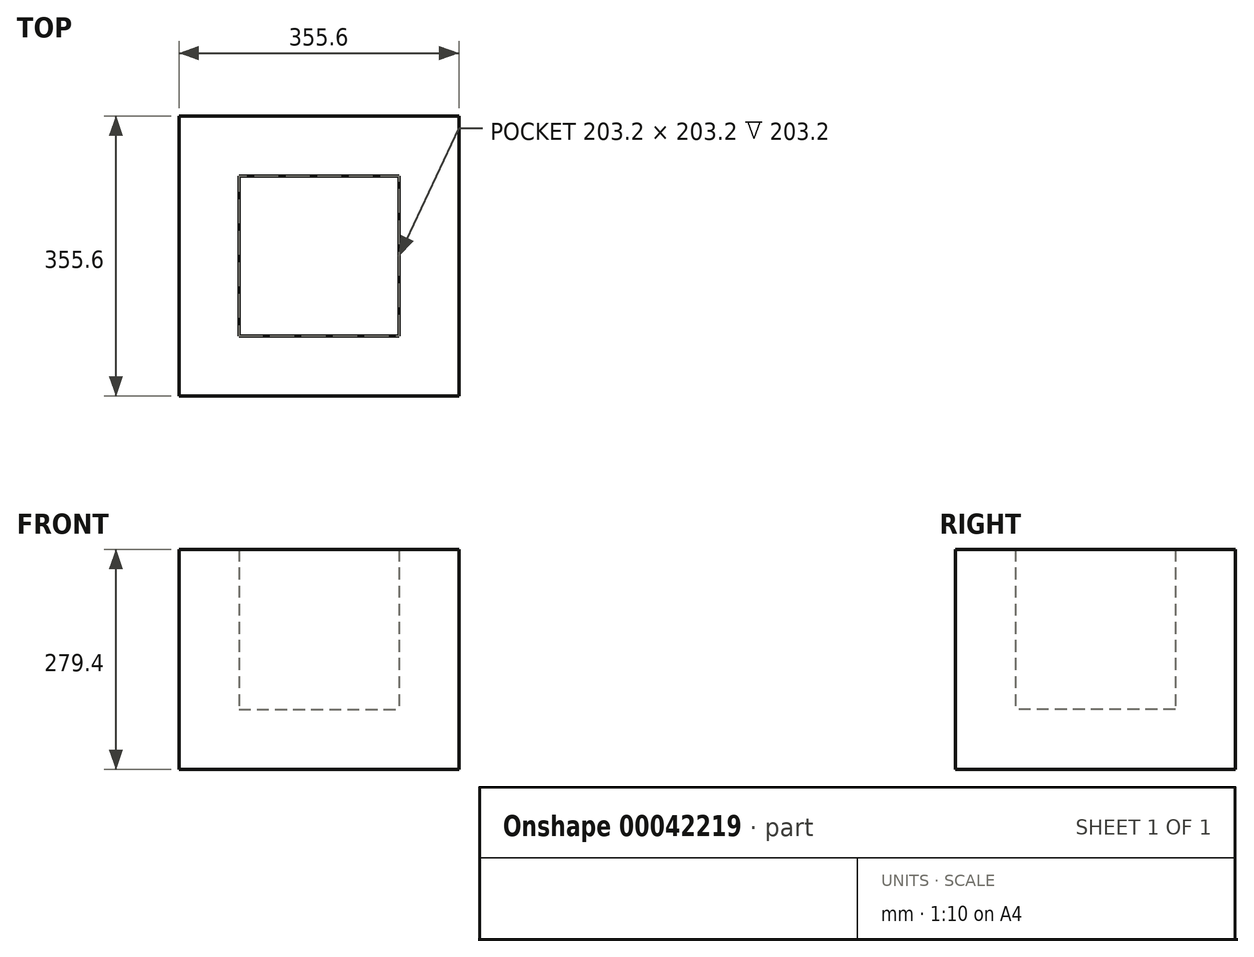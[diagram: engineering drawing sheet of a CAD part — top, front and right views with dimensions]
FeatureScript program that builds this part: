
annotation { "Feature Type Name" : "Feature", "Feature Type Description" : "" }
export const myFeature = defineFeature(function(context is Context, id is Id, definition is map)
    precondition{}
    {
        {
            var Q0;
            Q0=qCreatedBy(makeId("Top.planeOp"),FACE);
            var sketch = newSketch(context, id + "F0", { "sketchPlane" : qUnion([Q0])});
            skLineSegment(sketch, "E0.bottom", {"start": v(-154.17, 102.23) * mm, "end": v(49.03, 102.23) * mm});
            skLineSegment(sketch, "E0.top", {"start": v(-154.17, -100.97) * mm, "end": v(49.03, -100.97) * mm});
            skLineSegment(sketch, "E0.left", {"start": v(-154.17, 102.23) * mm, "end": v(-154.17, -100.97) * mm});
            skLineSegment(sketch, "E0.right", {"start": v(49.03, 102.23) * mm, "end": v(49.03, -100.97) * mm});
            skLineSegment(sketch, "E1.bottom", {"start": v(-230.37, 178.43) * mm, "end": v(125.23, 178.43) * mm});
            skLineSegment(sketch, "E1.top", {"start": v(-230.37, -177.17) * mm, "end": v(125.23, -177.17) * mm});
            skLineSegment(sketch, "E1.left", {"start": v(-230.37, 178.43) * mm, "end": v(-230.37, -177.17) * mm});
            skLineSegment(sketch, "E1.right", {"start": v(125.23, 178.43) * mm, "end": v(125.23, -177.17) * mm});
            skLineSegment(sketch, "E2", {"start": v(-154.17, 12.07) * mm, "end": v(-230.37, 12.07) * mm});
            skLineSegment(sketch, "E3", {"start": v(49.03, 6.1) * mm, "end": v(125.23, 6.1) * mm});
            skLineSegment(sketch, "E4", {"start": v(-52.57, -100.97) * mm, "end": v(-52.57, -177.17) * mm});
            skLineSegment(sketch, "E5", {"start": v(-52.57, 102.23) * mm, "end": v(-52.57, 178.43) * mm});
            skSolve(sketch);
        }
        {
            var Q0;
            {var subQ4=sQuery(id+"F0.wireOp",EDGE,"E2");Q0=makeQuery(id+"F0.imprint","IMPRINT",FACE,{"disambiguationData":[TD([[makeQuery(id+"F0.imprint","IMPRINT",EDGE,{"derivedFrom":subQ4}),-1.0]])]});}
            var Q1;
            {var subQ4=sQuery(id+"F0.wireOp",EDGE,"E2");Q1=makeQuery(id+"F0.imprint","IMPRINT",FACE,{"disambiguationData":[TD([[makeQuery(id+"F0.imprint","IMPRINT",EDGE,{"derivedFrom":subQ4}),1.0]])]});}
            var Q2;
            {var subQ0=sQuery(id+"F0.wireOp",EDGE,"E3");Q2=makeQuery(id+"F0.imprint","IMPRINT",FACE,{"disambiguationData":[TD([[makeQuery(id+"F0.imprint","IMPRINT",EDGE,{"derivedFrom":subQ0}),-1.0]])]});}
            var Q3;
            {var subQ4=sQuery(id+"F0.wireOp",EDGE,"E3");Q3=makeQuery(id+"F0.imprint","IMPRINT",FACE,{"disambiguationData":[TD([[makeQuery(id+"F0.imprint","IMPRINT",EDGE,{"derivedFrom":subQ4}),1.0]])]});}
            extrude(context, id + "F1", {"entities" : qUnion([Q0, Q1, Q2, Q3]), "depth" : 203.2 * mm});
        }
        {
            var Q0;
            Q0=makeQuery(id+"F1.opExtrude","CAP_FACE",FACE,{"disambiguationData":[OSD([sQuery(id+"F0.wireOp",EDGE,"E0.bottom"),sQuery(id+"F0.wireOp",EDGE,"E0.top"),sQuery(id+"F0.wireOp",EDGE,"E0.left"),sQuery(id+"F0.wireOp",EDGE,"E0.right"),sQuery(id+"F0.wireOp",EDGE,"E1.bottom"),sQuery(id+"F0.wireOp",EDGE,"E1.top"),sQuery(id+"F0.wireOp",EDGE,"E1.left"),sQuery(id+"F0.wireOp",EDGE,"E1.right")])],"isStart":true});
            var sketch = newSketch(context, id + "F2", { "sketchPlane" : qUnion([Q0])});
            skLineSegment(sketch, "E6.bottom", {"start": v(-230.37, -178.43) * mm, "end": v(125.23, -178.43) * mm});
            skLineSegment(sketch, "E6.top", {"start": v(-230.37, 177.17) * mm, "end": v(125.23, 177.17) * mm});
            skLineSegment(sketch, "E6.left", {"start": v(-230.37, -178.43) * mm, "end": v(-230.37, 177.17) * mm});
            skLineSegment(sketch, "E6.right", {"start": v(125.23, -178.43) * mm, "end": v(125.23, 177.17) * mm});
            skSolve(sketch);
        }
        {
            var Q0;
            Q0 = qSketchRegion(id + "F2", true);
            extrude(context, id + "F3", {"entities" : qUnion([Q0]), "operationType" : NewBodyOperationType.ADD, "depth" : 76.2 * mm});
        }
    });
